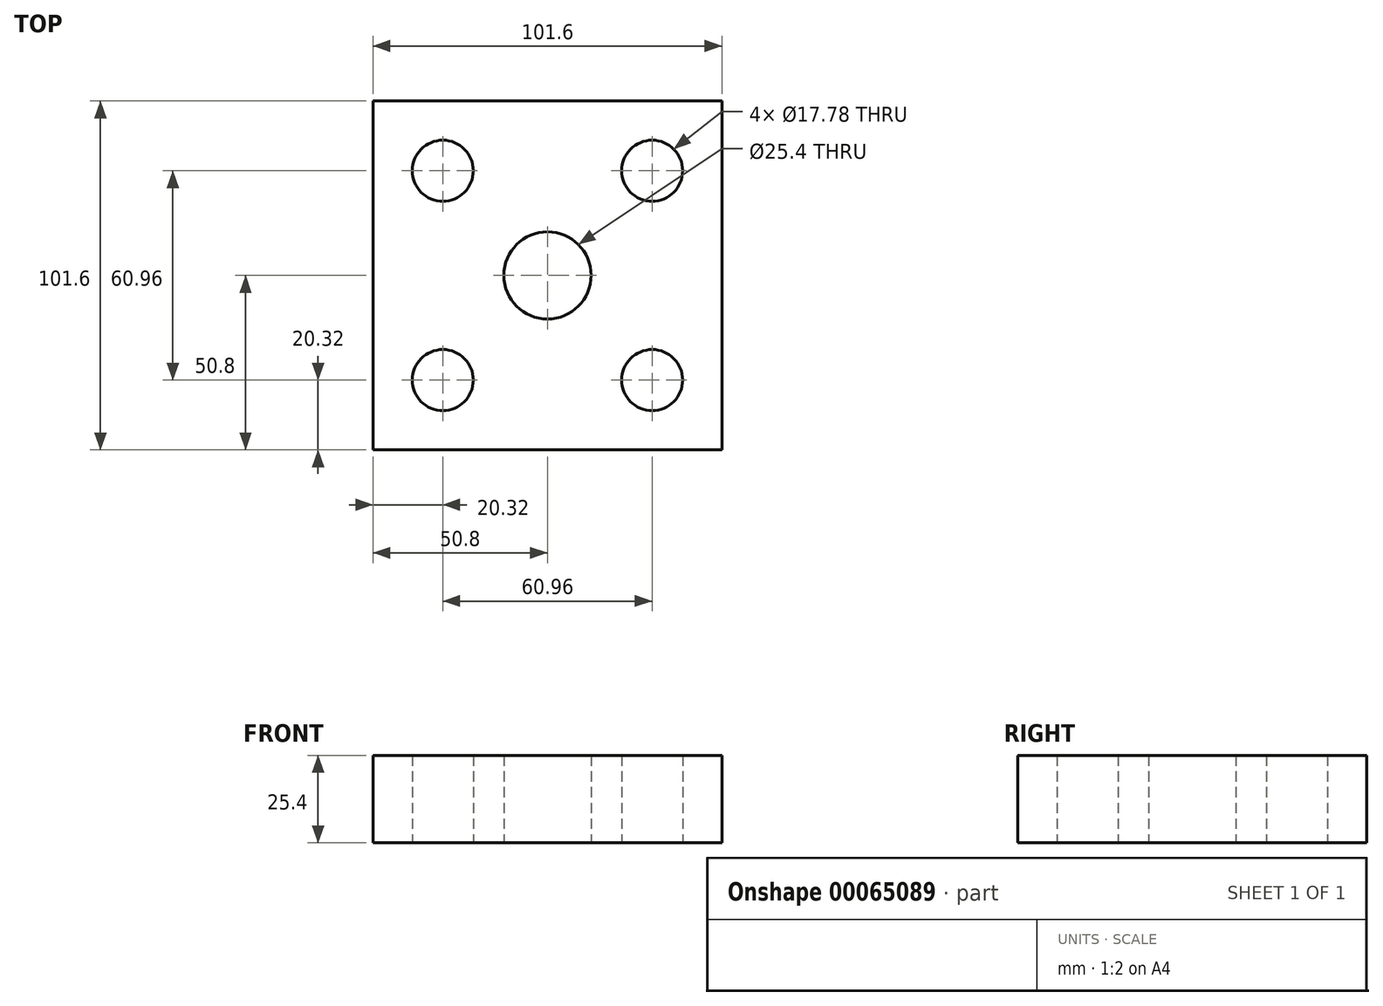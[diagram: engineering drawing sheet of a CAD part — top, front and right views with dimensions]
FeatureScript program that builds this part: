
annotation { "Feature Type Name" : "Feature", "Feature Type Description" : "" }
export const myFeature = defineFeature(function(context is Context, id is Id, definition is map)
    precondition{}
    {
        {
            var Q0;
            Q0=qCreatedBy(makeId("Top.planeOp"),FACE);
            var sketch = newSketch(context, id + "F0", { "sketchPlane" : qUnion([Q0])});
            skLineSegment(sketch, "E0.rect.bottom", {"start": v(50.8, 50.8) * mm, "end": v(-50.8, 50.8) * mm});
            skLineSegment(sketch, "E0.rect.top", {"start": v(50.8, -50.8) * mm, "end": v(-50.8, -50.8) * mm});
            skLineSegment(sketch, "E0.rect.left", {"start": v(50.8, 50.8) * mm, "end": v(50.8, -50.8) * mm});
            skLineSegment(sketch, "E0.rect.right", {"start": v(-50.8, 50.8) * mm, "end": v(-50.8, -50.8) * mm});
            skPoint(sketch, "E0.rect.middle", {"position": v(0, 0) * mm});
            skCircle(sketch, "E1", {"center": v(0, 0) * mm, "radius": 12.7 * mm});
            skCircle(sketch, "E2", {"center": v(30.48, 30.48) * mm, "radius": 8.9 * mm});
            skCircle(sketch, "E3", {"center": v(-30.48, 30.48) * mm, "radius": 8.9 * mm});
            skCircle(sketch, "E4", {"center": v(-30.48, -30.48) * mm, "radius": 8.9 * mm});
            skCircle(sketch, "E5", {"center": v(30.48, -30.48) * mm, "radius": 8.9 * mm});
            skSolve(sketch);
        }
        {
            var Q0;
            Q0=makeQuery(id+"F0.imprint","IMPRINT",FACE,{"disambiguationData":[TD([[makeQuery(id+"F0.imprint","IMPRINT",EDGE,{"derivedFrom":sQuery(id+"F0.wireOp",EDGE,"E0.rect.bottom")}),1.0]])]});
            extrude(context, id + "F1", {"entities" : qUnion([Q0]), "depth" : 25.4 * mm});
        }
    });
